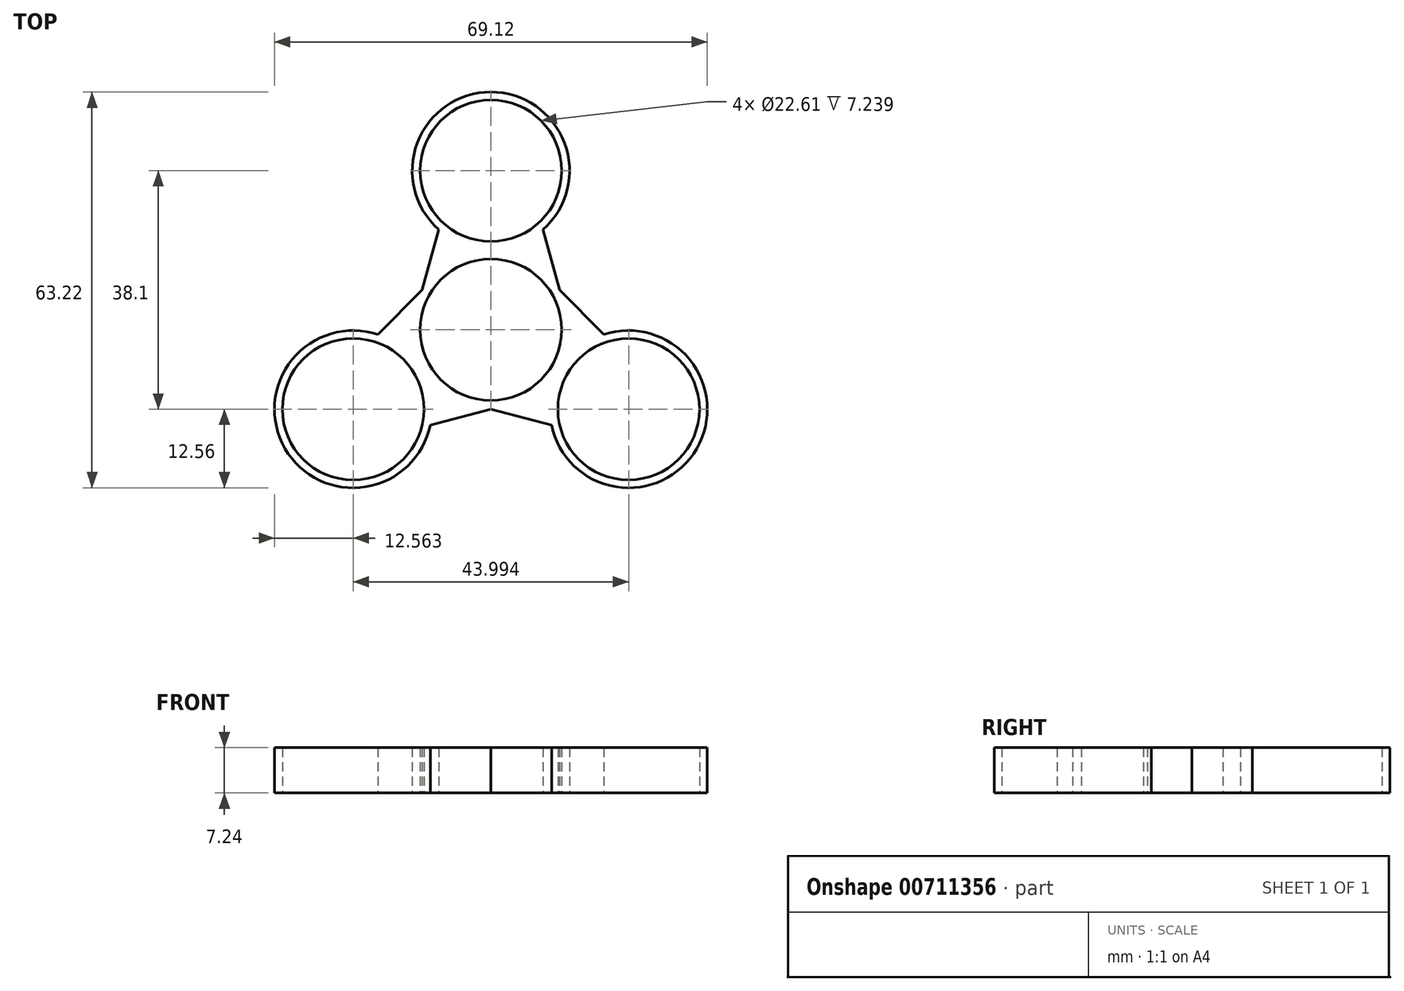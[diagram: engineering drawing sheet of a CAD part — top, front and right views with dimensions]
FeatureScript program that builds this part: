
annotation { "Feature Type Name" : "Feature", "Feature Type Description" : "" }
export const myFeature = defineFeature(function(context is Context, id is Id, definition is map)
    precondition{}
    {
        {
            var Q0;
            Q0=qCreatedBy(makeId("Top.planeOp"),FACE);
            var sketch = newSketch(context, id + "F0", { "sketchPlane" : qUnion([Q0])});
            skCircle(sketch, "E0", {"center": v(0, 0) * mm, "radius": 12.7 * mm});
            skCircle(sketch, "E1", {"center": v(0, 25.4) * mm, "radius": 12.56 * mm});
            skCircle(sketch, "E2", {"center": v(0, 25.4) * mm, "radius": 11.3 * mm});
            skCircle(sketch, "E3.1.0", {"center": v(-22, -12.7) * mm, "radius": 11.3 * mm});
            skCircle(sketch, "E3.1.1", {"center": v(-22, -12.7) * mm, "radius": 12.56 * mm});
            skCircle(sketch, "E3.2.0", {"center": v(22, -12.7) * mm, "radius": 11.3 * mm});
            skCircle(sketch, "E3.2.1", {"center": v(22, -12.7) * mm, "radius": 12.56 * mm});
            skLineSegment(sketch, "E4", {"start": v(0, -12.7) * mm, "end": v(9.69, -15.2) * mm});
            skLineSegment(sketch, "E5", {"start": v(-9.69, -15.2) * mm, "end": v(0, -12.7) * mm});
            skLineSegment(sketch, "E6.1.0", {"start": v(18.02, -0.78) * mm, "end": v(11, 6.35) * mm});
            skLineSegment(sketch, "E6.1.1", {"start": v(11, 6.35) * mm, "end": v(8.33, 16) * mm});
            skLineSegment(sketch, "E6.2.0", {"start": v(-8.33, 16) * mm, "end": v(-11, 6.35) * mm});
            skLineSegment(sketch, "E6.2.1", {"start": v(-11, 6.35) * mm, "end": v(-18.02, -0.78) * mm});
            skCircle(sketch, "E7", {"center": v(0, 0) * mm, "radius": 11.3 * mm});
            skSolve(sketch);
        }
        {
            var Q0;
            Q0=makeQuery(id+"F0.imprint","IMPRINT",FACE,{"disambiguationData":[TD([[makeQuery(id+"F0.imprint","IMPRINT",EDGE,{"derivedFrom":sQuery(id+"F0.wireOp",EDGE,"E2")}),-1.0]])]});
            var Q1;
            Q1=makeQuery(id+"F0.imprint","IMPRINT",FACE,{"disambiguationData":[TD([[makeQuery(id+"F0.imprint","IMPRINT",EDGE,{"derivedFrom":sQuery(id+"F0.wireOp",EDGE,"E2")}),1.0]])]});
            var Q2;
            {var subQ0=sQuery(id+"F0.wireOp",EDGE,"E4");Q2=makeQuery(id+"F0.imprint","IMPRINT",FACE,{"disambiguationData":[TD([[makeQuery(id+"F0.imprint","IMPRINT",EDGE,{"derivedFrom":subQ0}),1.0]])]});}
            var Q3;
            {var subQ0=sQuery(id+"F0.wireOp",EDGE,"E6.1.1");Q3=makeQuery(id+"F0.imprint","IMPRINT",FACE,{"disambiguationData":[TD([[makeQuery(id+"F0.imprint","IMPRINT",EDGE,{"derivedFrom":subQ0}),1.0]])]});}
            var Q4;
            Q4=makeQuery(id+"F0.imprint","IMPRINT",FACE,{"disambiguationData":[TD([[makeQuery(id+"F0.imprint","IMPRINT",EDGE,{"derivedFrom":sQuery(id+"F0.wireOp",EDGE,"E3.1.0")}),1.0]])]});
            var Q5;
            Q5=makeQuery(id+"F0.imprint","IMPRINT",FACE,{"disambiguationData":[TD([[makeQuery(id+"F0.imprint","IMPRINT",EDGE,{"derivedFrom":sQuery(id+"F0.wireOp",EDGE,"E3.2.0")}),1.0]])]});
            var Q6;
            Q6=makeQuery(id+"F0.imprint","IMPRINT",FACE,{"disambiguationData":[TD([[makeQuery(id+"F0.imprint","IMPRINT",EDGE,{"derivedFrom":sQuery(id+"F0.wireOp",EDGE,"E7")}),-1.0]])]});
            var Q7;
            Q7=makeQuery(id+"F0.imprint","IMPRINT",FACE,{"disambiguationData":[TD([[makeQuery(id+"F0.imprint","IMPRINT",EDGE,{"derivedFrom":sQuery(id+"F0.wireOp",EDGE,"E7")}),1.0]])]});
            var Q8;
            Q8=makeQuery(id+"F0.imprint","IMPRINT",FACE,{"disambiguationData":[TD([[makeQuery(id+"F0.imprint","IMPRINT",EDGE,{"derivedFrom":sQuery(id+"F0.wireOp",EDGE,"E3.2.0")}),-1.0]])]});
            var Q9;
            Q9=makeQuery(id+"F0.imprint","IMPRINT",FACE,{"disambiguationData":[TD([[makeQuery(id+"F0.imprint","IMPRINT",EDGE,{"derivedFrom":sQuery(id+"F0.wireOp",EDGE,"E3.1.0")}),-1.0]])]});
            var Q10;
            {var subQ0=sQuery(id+"F0.wireOp",EDGE,"E5");Q10=makeQuery(id+"F0.imprint","IMPRINT",FACE,{"disambiguationData":[TD([[makeQuery(id+"F0.imprint","IMPRINT",EDGE,{"derivedFrom":subQ0}),1.0]])]});}
            extrude(context, id + "F1", {"entities" : qUnion([Q0, Q1, Q2, Q3, Q4, Q5, Q6, Q7, Q8, Q9, Q10]), "depth" : 7.24 * mm, "offsetDistance" : 25.4 * mm});
        }
        {
            var Q0;
            Q0=makeQuery(id+"F0.imprint","IMPRINT",FACE,{"disambiguationData":[TD([[makeQuery(id+"F0.imprint","IMPRINT",EDGE,{"derivedFrom":sQuery(id+"F0.wireOp",EDGE,"E3.2.0")}),1.0]])]});
            var Q1;
            Q1=makeQuery(id+"F0.imprint","IMPRINT",FACE,{"disambiguationData":[TD([[makeQuery(id+"F0.imprint","IMPRINT",EDGE,{"derivedFrom":sQuery(id+"F0.wireOp",EDGE,"E7")}),1.0]])]});
            var Q2;
            Q2=makeQuery(id+"F0.imprint","IMPRINT",FACE,{"disambiguationData":[TD([[makeQuery(id+"F0.imprint","IMPRINT",EDGE,{"derivedFrom":sQuery(id+"F0.wireOp",EDGE,"E2")}),1.0]])]});
            var Q3;
            Q3=makeQuery(id+"F0.imprint","IMPRINT",FACE,{"disambiguationData":[TD([[makeQuery(id+"F0.imprint","IMPRINT",EDGE,{"derivedFrom":sQuery(id+"F0.wireOp",EDGE,"E3.1.0")}),1.0]])]});
            extrude(context, id + "F2", {"entities" : qUnion([Q0, Q1, Q2, Q3]), "operationType" : NewBodyOperationType.REMOVE, "depth" : 25.4 * mm, "offsetDistance" : 25.4 * mm});
        }
    });
